# Revit family: BuzziSpace - BuzziChip
name_source: partatom
category: Lighting Fixtures
units: mm (PartAtom-declared; Revit-internal decimal feet)

## family parameters
Always vertical = Yes
Cut with Voids When Loaded = No
Host = Ceiling
Light Source = No
OmniClass Number = 23.80.70.11
OmniClass Title = Luminaries for Internal Lighting
Part Type = Normal
Room Calculation Point = No
Round Connector Dimension = Use Diameter
Shared = No

## types (9) — shared parameters
Light Spacing = 38 cm
Manufacturer = BuzziSpace
Small Lights = Yes

## per-type parameters (varying)
| type | Bar Length | Cable Spacing | Globe | Large Lights | Length | Medium Lights | Model | Retrofit | Spot |
| Small - Globe | 83 cm | 48 cm | Yes | No | 70 cm | No | BuzziChip Small | No | No |
| Medium - Globe | 83 cm | 75 cm | Yes | No | 140 cm | Yes | BuzziChip Medium | No | No |
| Large - Globe | 157 cm | 150 cm | Yes | Yes | 210 cm | Yes | BuzziChip Large | No | No |
| Small - Spot | 83 cm | 48 cm | No | No | 70 cm | No | BuzziChip Small | No | Yes |
| Medium - Spot | 83 cm | 75 cm | No | No | 140 cm | Yes | BuzziChip Medium | No | Yes |
| Large - Spot | 157 cm | 150 cm | No | Yes | 210 cm | Yes | BuzziChip Large | No | Yes |
| Small - Retrofit | 83 cm | 48 cm | No | No | 70 cm | No | BuzziChip Small | Yes | No |
| Medium - Retrofit | 83 cm | 75 cm | No | No | 140 cm | Yes | BuzziChip Medium | Yes | No |
| Large - Retrofit | 157 cm | 150 cm | No | Yes | 210 cm | Yes | BuzziChip Large | Yes | No |

## geometry (parser evidence)
native form markers: Sweep x15
no freeform markers — native parametric forms only
